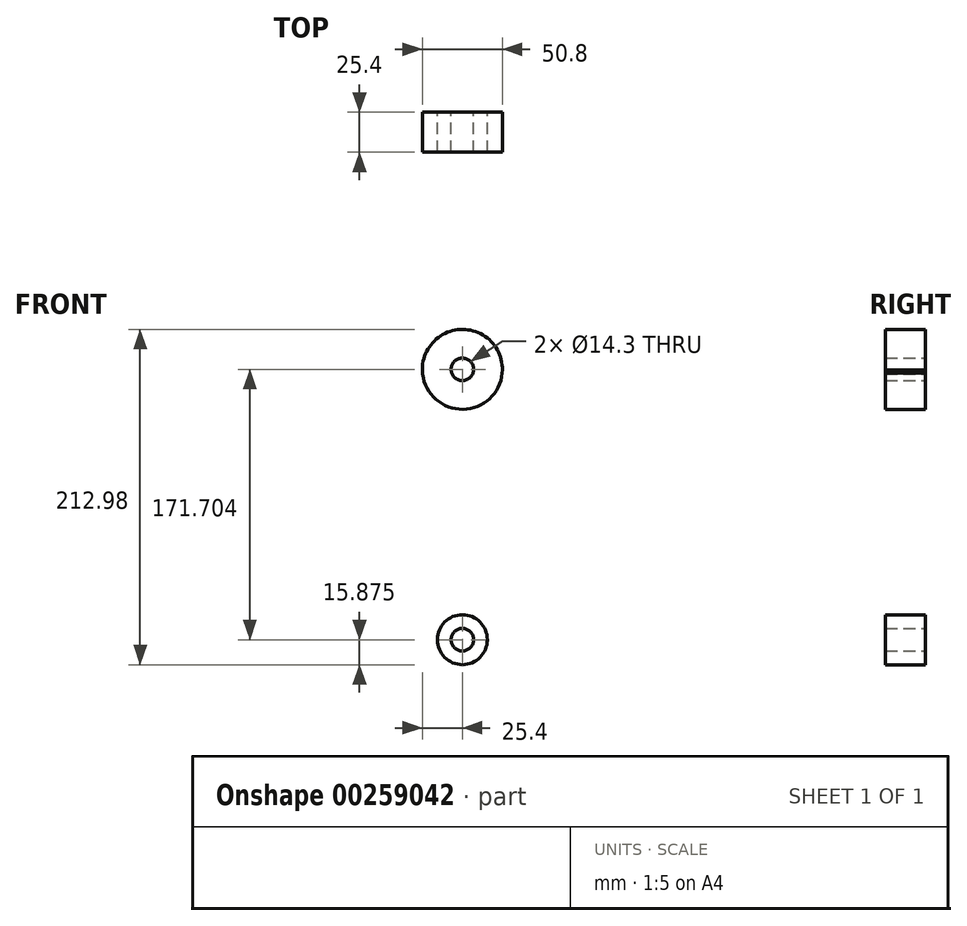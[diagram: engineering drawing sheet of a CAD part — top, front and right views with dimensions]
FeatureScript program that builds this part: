
annotation { "Feature Type Name" : "Feature", "Feature Type Description" : "" }
export const myFeature = defineFeature(function(context is Context, id is Id, definition is map)
    precondition{}
    {
        {
            var Q0;
            Q0=qCreatedBy(makeId("Front.planeOp"),FACE);
            var sketch = newSketch(context, id + "F0", { "sketchPlane" : qUnion([Q0])});
            skCircle(sketch, "E0", {"center": v(0, 130.75) * mm, "radius": 25.4 * mm});
            skCircle(sketch, "E1", {"center": v(0, -40.96) * mm, "radius": 15.88 * mm});
            skCircle(sketch, "E2", {"center": v(0, 130.75) * mm, "radius": 7.15 * mm});
            skCircle(sketch, "E3", {"center": v(0, -40.96) * mm, "radius": 7.15 * mm});
            skLineSegment(sketch, "E4", {"start": v(-25.4, 130.9) * mm, "end": v(-15.85, -41.83) * mm});
            skLineSegment(sketch, "E5", {"start": v(25.4, 130.27) * mm, "end": v(15.85, -41.83) * mm});
            skSolve(sketch);
        }
        {
            var Q0;
            {var subQ0=sQuery(id+"F0.wireOp",EDGE,"E4");var subQ1=sQuery(id+"F0.wireOp",EDGE,"E0");var subQ2=makeQuery(id+"F0.imprint","INTERSECT",VERTEX,{"disambiguationData":[OD(1.0)],"derivedFrom":[subQ1,subQ0]});Q0=makeQuery(id+"F0.imprint","IMPRINT",FACE,{"disambiguationData":[TD([[makeQuery(id+"F0.imprint","IMPRINT",EDGE,{"disambiguationData":[TD([[subQ2,-1.0]])],"derivedFrom":subQ1}),-1.0]])]});}
            var Q1;
            Q1=makeQuery(id+"F0.imprint","IMPRINT",FACE,{"disambiguationData":[TD([[makeQuery(id+"F0.imprint","IMPRINT",EDGE,{"derivedFrom":sQuery(id+"F0.wireOp",EDGE,"E2")}),-1.0]])]});
            var Q2;
            Q2=makeQuery(id+"F0.imprint","IMPRINT",FACE,{"disambiguationData":[TD([[makeQuery(id+"F0.imprint","IMPRINT",EDGE,{"derivedFrom":sQuery(id+"F0.wireOp",EDGE,"E3")}),-1.0]])]});
            extrude(context, id + "F1", {"entities" : qUnion([Q0, Q1, Q2]), "depth" : 25.4 * mm});
        }
    });
